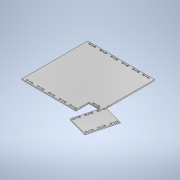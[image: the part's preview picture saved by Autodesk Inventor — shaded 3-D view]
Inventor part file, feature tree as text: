
AUTODESK INVENTOR PART (.ipt)
format: ipt  version: 2020.1 (Build 241239000, 239)  size: 686,080 bytes
history: native  units: mm
features: other x22, extrude x1, sketch x1
ambient origin geometry x8: Origin, YZ Plane, XZ Plane, XY Plane, X Axis, Y Axis, Z Axis, Center Point
bodies: Body1 (feature_tree)
feature tree (24):
  other  "shared_parameters.ipt"
  other  "Blocs"
  extrude  "Extrusion2"  Depth=10.0mm
  other  "Anchor (screw side)"
  other  "Anchor (nut side)"
  sketch  "Esquisse2"
  other  "Anchor (screw side):1"
  other  "Anchor (screw side):2"
  other  "Anchor (screw side):3"
  other  "Anchor (screw side):4"
  other  "Anchor (screw side):5"
  other  "Anchor (screw side):6"
  other  "Anchor (screw side):7"
  other  "Anchor (screw side):8"
  other  "Anchor (screw side):9"
  other  "Anchor (screw side):10"
  other  "Anchor (screw side):11"
  other  "Anchor (screw side):12"
  other  "Anchor (screw side):13"
  other  "Anchor (screw side):14"
  other  "Anchor (screw side):15"
  other  "Anchor (screw side):16"
  other  "Anchor (screw side):17"
  other  "Anchor (screw side):18"
